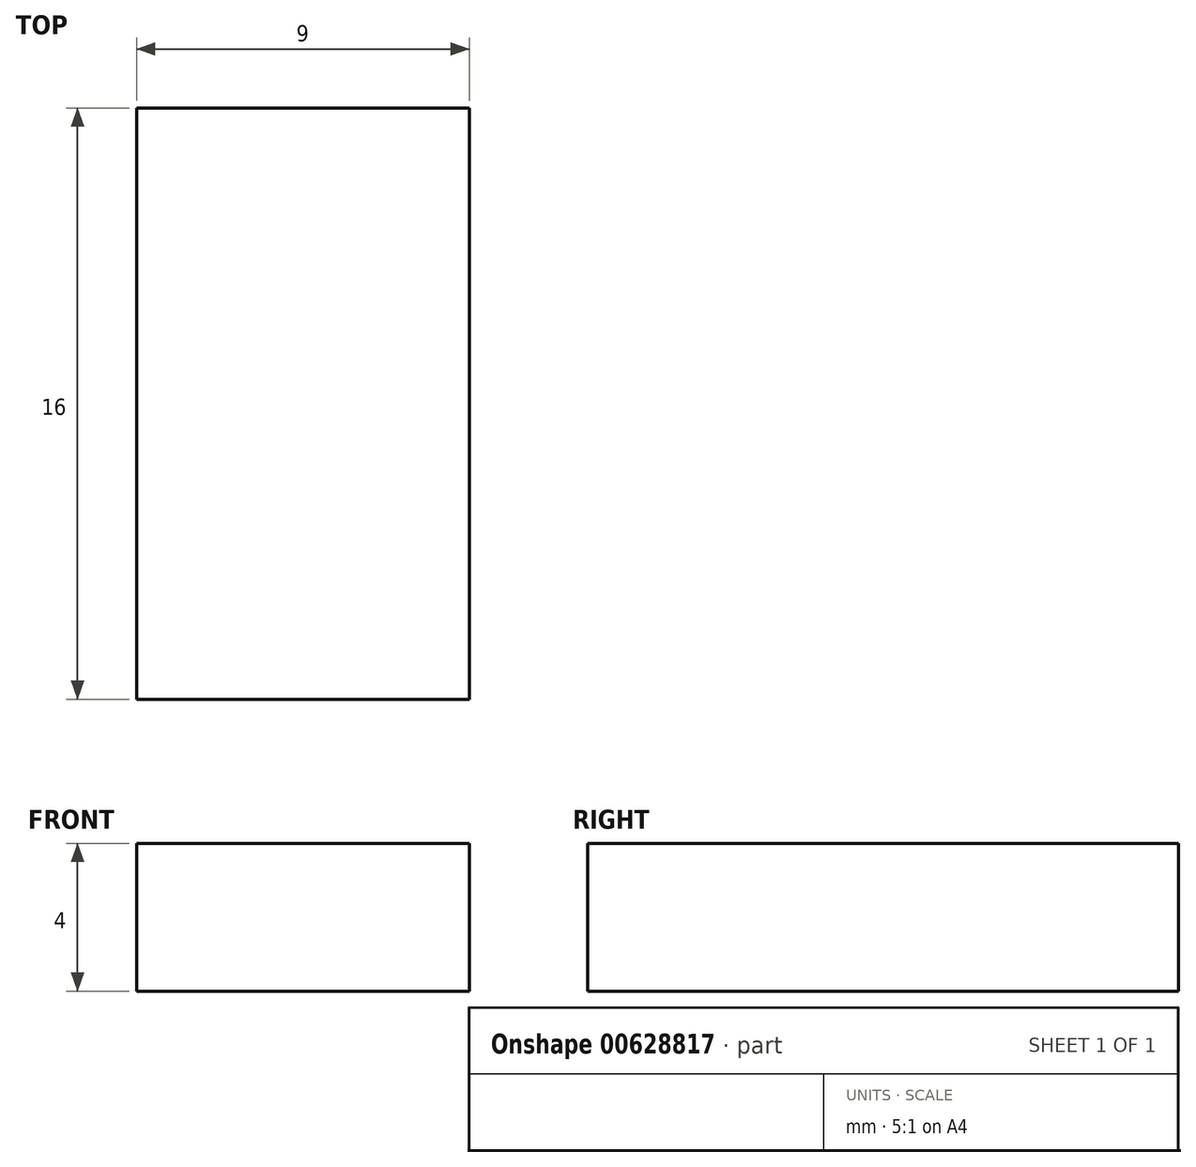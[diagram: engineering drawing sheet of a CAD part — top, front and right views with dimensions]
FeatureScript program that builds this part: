
annotation { "Feature Type Name" : "Feature", "Feature Type Description" : "" }
export const myFeature = defineFeature(function(context is Context, id is Id, definition is map)
    precondition{}
    {
        {
            var Q0;
            Q0=qCreatedBy(makeId("Top.planeOp"),FACE);
            var sketch = newSketch(context, id + "F0", { "sketchPlane" : qUnion([Q0])});
            skLineSegment(sketch, "E0.bottom", {"start": v(4.5, 8) * mm, "end": v(-4.5, 8) * mm});
            skLineSegment(sketch, "E0.top", {"start": v(4.5, -8) * mm, "end": v(-4.5, -8) * mm});
            skLineSegment(sketch, "E0.left", {"start": v(4.5, 8) * mm, "end": v(4.5, -8) * mm});
            skLineSegment(sketch, "E0.right", {"start": v(-4.5, 8) * mm, "end": v(-4.5, -8) * mm});
            skPoint(sketch, "E0.middle", {"position": v(0, 0) * mm});
            skSolve(sketch);
        }
        {
            var Q0;
            Q0 = qSketchRegion(id + "F0", true);
            extrude(context, id + "F1", {"entities" : qUnion([Q0]), "depth" : 4 * mm, "offsetDistance" : 25 * mm, "symmetric" : true});
        }
    });
